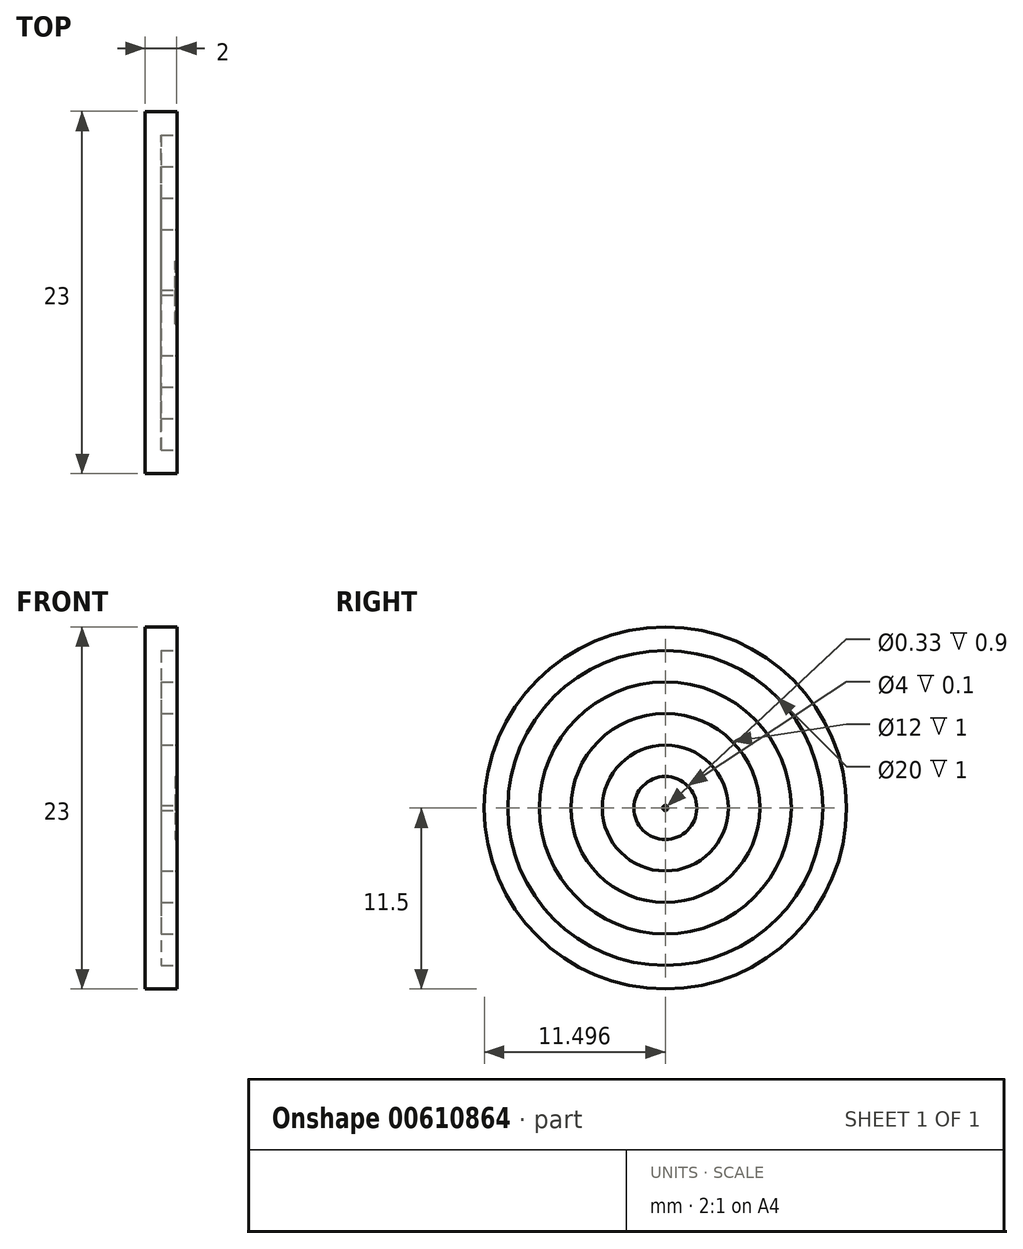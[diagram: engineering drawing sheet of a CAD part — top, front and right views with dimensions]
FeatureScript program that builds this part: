
annotation { "Feature Type Name" : "Feature", "Feature Type Description" : "" }
export const myFeature = defineFeature(function(context is Context, id is Id, definition is map)
    precondition{}
    {
        {
            var Q0;
            Q0=qCreatedBy(makeId("Top.planeOp"),FACE);
            var sketch = newSketch(context, id + "F0", { "sketchPlane" : qUnion([Q0])});
            skLineSegment(sketch, "E0.bottom", {"start": v(-17.23, 13.5) * mm, "end": v(-16.23, 13.5) * mm});
            skLineSegment(sketch, "E0.top", {"start": v(-17.23, 2) * mm, "end": v(-16.23, 2) * mm});
            skLineSegment(sketch, "E0.left", {"start": v(-17.23, 13.5) * mm, "end": v(-17.23, 2) * mm});
            skLineSegment(sketch, "E0.right", {"start": v(-16.23, 13.5) * mm, "end": v(-16.23, 2) * mm});
            skLineSegment(sketch, "E1.bottom", {"start": v(-6.98, 2) * mm, "end": v(-15.23, 2) * mm, "construction": true});
            skLineSegment(sketch, "E1.top", {"start": v(-6.98, 2) * mm, "end": v(-15.23, 2) * mm, "construction": true});
            skLineSegment(sketch, "E1.left", {"start": v(-6.98, 2) * mm, "end": v(-6.98, 2) * mm});
            skLineSegment(sketch, "E1.right", {"start": v(-33.05, 2) * mm, "end": v(-33.05, 2) * mm});
            skLineSegment(sketch, "E2.bottom", {"start": v(-16.23, 2) * mm, "end": v(-15.23, 2) * mm});
            skLineSegment(sketch, "E2.top", {"start": v(-16.23, 4) * mm, "end": v(-15.33, 4) * mm});
            skLineSegment(sketch, "E2.left", {"start": v(-16.23, 2) * mm, "end": v(-16.23, 4) * mm});
            skLineSegment(sketch, "E3.left", {"start": v(-16.23, 4) * mm, "end": v(-16.23, 6) * mm});
            skLineSegment(sketch, "E4.left", {"start": v(-16.23, 6) * mm, "end": v(-16.23, 8) * mm});
            skPoint(sketch, "E5.oppositeSnap0", {"position": v(-15.23, 8) * mm});
            skLineSegment(sketch, "E5.left", {"start": v(-16.23, 8) * mm, "end": v(-16.23, 10) * mm});
            skLineSegment(sketch, "E6.left", {"start": v(-16.23, 10) * mm, "end": v(-16.23, 12) * mm});
            skPoint(sketch, "E7.oppositeSnap0", {"position": v(-16.73, 13.5) * mm});
            skPoint(sketch, "E7.right.end.orphan", {"position": v(-12.58, 13.5) * mm});
            skPoint(sketch, "E7.left.end.orphan", {"position": v(-13.58, 16.7) * mm});
            skLineSegment(sketch, "E8.trimOffspring", {"start": v(-16.23, 2) * mm, "end": v(-33.05, 2) * mm, "construction": true});
            skLineSegment(sketch, "E9", {"start": v(-15.33, 4) * mm, "end": v(-15.23, 4) * mm});
            skLineSegment(sketch, "E10", {"start": v(-15.23, 2) * mm, "end": v(-15.23, 2.16) * mm});
            skPoint(sketch, "E11.orphan", {"position": v(-14.23, 8) * mm});
            skLineSegment(sketch, "E12", {"start": v(-15.33, 6) * mm, "end": v(-15.23, 6) * mm});
            skLineSegment(sketch, "E13", {"start": v(-15.25, 8) * mm, "end": v(-15.23, 8) * mm});
            skPoint(sketch, "E5.top.end.orphan", {"position": v(-15.23, 10) * mm});
            skPoint(sketch, "E14.start.orphan", {"position": v(-15.28, 13.5) * mm});
            skLineSegment(sketch, "E15", {"start": v(-16.23, 13.5) * mm, "end": v(-15.23, 13.5) * mm});
            skLineSegment(sketch, "E16", {"start": v(-15.23, 13.5) * mm, "end": v(-15.23, 12) * mm});
            skLineSegment(sketch, "E17", {"start": v(-16.23, 12) * mm, "end": v(-15.23, 12) * mm});
            skLineSegment(sketch, "E18", {"start": v(-16.23, 10) * mm, "end": v(-15.23, 10) * mm});
            skLineSegment(sketch, "E19", {"start": v(-16.23, 8) * mm, "end": v(-15.23, 8) * mm});
            skLineSegment(sketch, "E20", {"start": v(-16.23, 6) * mm, "end": v(-15.33, 6) * mm});
            skLineSegment(sketch, "E21", {"start": v(-16.23, 12) * mm, "end": v(-15.33, 12) * mm});
            skLineSegment(sketch, "E22", {"start": v(-15.33, 12) * mm, "end": v(-15.33, 10) * mm});
            skLineSegment(sketch, "E23", {"start": v(-15.23, 8) * mm, "end": v(-15.33, 8) * mm});
            skLineSegment(sketch, "E24", {"start": v(-15.33, 8) * mm, "end": v(-15.33, 6) * mm});
            skLineSegment(sketch, "E25", {"start": v(-15.33, 4) * mm, "end": v(-15.33, 2.16) * mm});
            skLineSegment(sketch, "E26", {"start": v(-15.33, 2.16) * mm, "end": v(-16.23, 2.16) * mm});
            skLineSegment(sketch, "E27", {"start": v(-16.23, 2.16) * mm, "end": v(-15.33, 2.16) * mm});
            skLineSegment(sketch, "E28", {"start": v(-15.23, 2.16) * mm, "end": v(-15.33, 2.16) * mm});
            skLineSegment(sketch, "E29.trimOffspring", {"start": v(-15.23, 2.16) * mm, "end": v(-15.23, 2) * mm});
            skLineSegment(sketch, "E30", {"start": v(-16.23, 4) * mm, "end": v(-16.23, 2) * mm});
            skLineSegment(sketch, "E31", {"start": v(-15.23, 4) * mm, "end": v(-15.23, 6) * mm});
            skLineSegment(sketch, "E32", {"start": v(-15.23, 6) * mm, "end": v(-15.23, 4) * mm});
            skLineSegment(sketch, "E33", {"start": v(-15.23, 4) * mm, "end": v(-15.33, 4) * mm});
            skLineSegment(sketch, "E34", {"start": v(-15.23, 8) * mm, "end": v(-15.23, 10) * mm});
            skLineSegment(sketch, "E35", {"start": v(-16.23, 10) * mm, "end": v(-16.23, 8) * mm});
            skLineSegment(sketch, "E36", {"start": v(-15.23, 12) * mm, "end": v(-15.23, 13.5) * mm});
            skLineSegment(sketch, "E37", {"start": v(-16.23, 13.5) * mm, "end": v(-16.23, 10) * mm});
            skLineSegment(sketch, "E38", {"start": v(-16.23, 2) * mm, "end": v(-17.23, 2) * mm});
            skLineSegment(sketch, "E39.trimOffspring", {"start": v(-15.23, 10) * mm, "end": v(-15.23, 8) * mm});
            skLineSegment(sketch, "E40", {"start": v(-15.28, 13.5) * mm, "end": v(-15.23, 13.5) * mm});
            skLineSegment(sketch, "E41", {"start": v(-15.28, 13.5) * mm, "end": v(-16.23, 13.5) * mm});
            skSolve(sketch);
        }
        {
            var Q0;
            Q0=makeQuery(id+"F0.imprint","IMPRINT",FACE,{"disambiguationData":[TD([[makeQuery(id+"F0.imprint","IMPRINT",EDGE,{"derivedFrom":sQuery(id+"F0.wireOp",EDGE,"E17")}),1.0]])]});
            var Q1;
            Q1=makeQuery(id+"F0.imprint","IMPRINT",FACE,{"disambiguationData":[TD([[makeQuery(id+"F0.imprint","IMPRINT",EDGE,{"derivedFrom":sQuery(id+"F0.wireOp",EDGE,"E2.top")}),1.0]])]});
            var Q2;
            Q2=makeQuery(id+"F0.imprint","IMPRINT",FACE,{"disambiguationData":[TD([[makeQuery(id+"F0.imprint","IMPRINT",EDGE,{"derivedFrom":sQuery(id+"F0.wireOp",EDGE,"E4.left")}),-1.0]])]});
            var Q3;
            {var subQ0=sQuery(id+"F0.wireOp",EDGE,"E2.top");Q3=makeQuery(id+"F0.imprint","IMPRINT",FACE,{"disambiguationData":[TD([[makeQuery(id+"F0.imprint","IMPRINT",EDGE,{"derivedFrom":subQ0}),-1.0]])]});}
            var Q4;
            {var subQ0=sQuery(id+"F0.wireOp",EDGE,"E19");Q4=makeQuery(id+"F0.imprint","IMPRINT",FACE,{"disambiguationData":[TD([[makeQuery(id+"F0.imprint","IMPRINT",EDGE,{"derivedFrom":subQ0}),1.0]])]});}
            var Q5;
            {var subQ4=sQuery(id+"F0.wireOp",EDGE,"E21");Q5=makeQuery(id+"F0.imprint","IMPRINT",FACE,{"disambiguationData":[TD([[makeQuery(id+"F0.imprint","IMPRINT",EDGE,{"derivedFrom":subQ4}),-1.0]])]});}
            var Q6;
            {var subQ7=sQuery(id+"F0.wireOp",EDGE,"E0.bottom");Q6=makeQuery(id+"F0.imprint","IMPRINT",FACE,{"disambiguationData":[TD([[makeQuery(id+"F0.imprint","IMPRINT",EDGE,{"derivedFrom":subQ7}),-1.0]])]});}
            var Q7;
            {var subQ1=sQuery(id+"F0.wireOp",EDGE,"E27");Q7=makeQuery(id+"F0.imprint","IMPRINT",FACE,{"disambiguationData":[TD([[makeQuery(id+"F0.imprint","IMPRINT",EDGE,{"derivedFrom":subQ1}),-1.0]])]});}
            var Q8;
            Q8=sQuery(id+"F0.wireOp",EDGE,"E8.trimOffspring");
            revolve(context, id + "F1", {"entities" : qUnion([Q0, Q1, Q2, Q3, Q4, Q5, Q6, Q7]), "axis" : qUnion([Q8]), "revolveType" : RevolveType.FULL});
        }
        {
            var Q0;
            Q0=makeQuery(id+"F1.opRevolve","SWEPT_BODY",BODY,{"disambiguationData":[OSD([sQuery(id+"F0.wireOp",EDGE,"E0.bottom"),sQuery(id+"F0.wireOp",EDGE,"E12"),sQuery(id+"F0.wireOp",EDGE,"E17"),sQuery(id+"F0.wireOp",EDGE,"E18"),sQuery(id+"F0.wireOp",EDGE,"E22"),sQuery(id+"F0.wireOp",EDGE,"E23"),sQuery(id+"F0.wireOp",EDGE,"E24"),sQuery(id+"F0.wireOp",EDGE,"E25"),sQuery(id+"F0.wireOp",EDGE,"E28"),sQuery(id+"F0.wireOp",EDGE,"E2.bottom"),sQuery(id+"F0.wireOp",EDGE,"E10"),sQuery(id+"F0.wireOp",EDGE,"E32"),sQuery(id+"F0.wireOp",EDGE,"E33"),sQuery(id+"F0.wireOp",EDGE,"E0.left"),sQuery(id+"F0.wireOp",EDGE,"E38"),sQuery(id+"F0.wireOp",EDGE,"E39.trimOffspring"),sQuery(id+"F0.wireOp",EDGE,"E40"),sQuery(id+"F0.wireOp",EDGE,"E41"),sQuery(id+"F0.wireOp",EDGE,"E36")])]});
            var Q1;
            Q1=sQuery(id+"F0.wireOp",EDGE,"E1.top");
            transform(context, id + "F2", {"entities" : qUnion([Q0]), "transformType" : TransformType.ROTATION, "transformAxis" : qUnion([Q1]), "angle" : 90 * degree, "oppositeDirection" : true, "makeCopy" : false});
        }
    });
